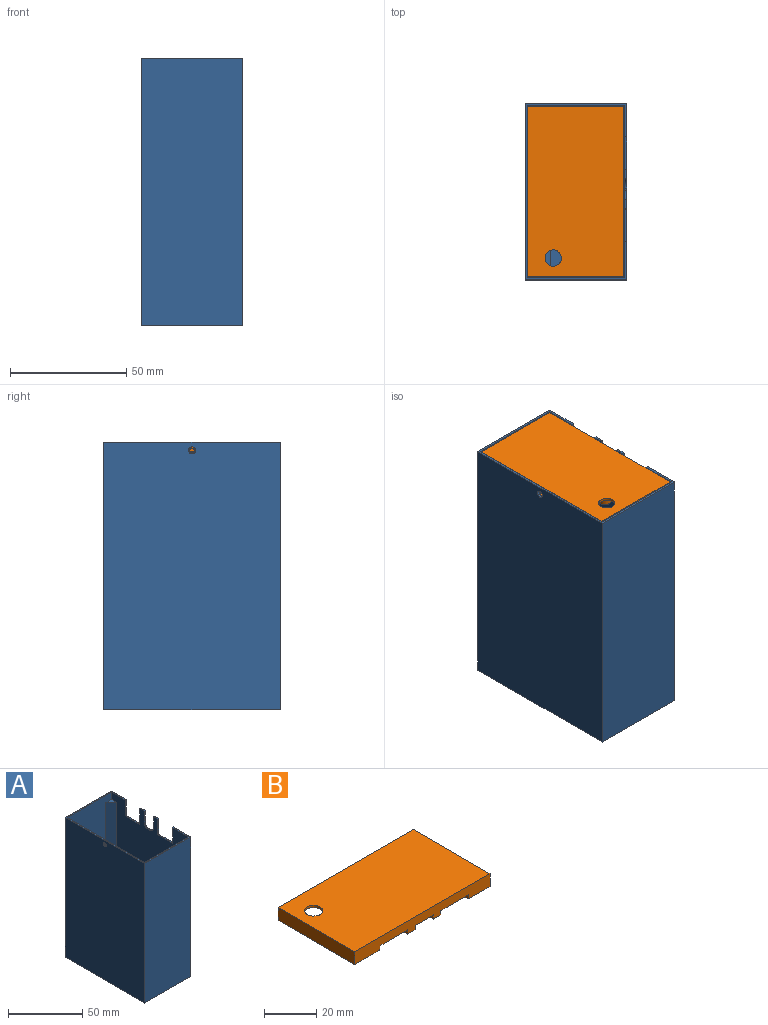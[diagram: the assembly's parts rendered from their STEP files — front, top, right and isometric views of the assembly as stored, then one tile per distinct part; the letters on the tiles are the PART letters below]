
ASSEMBLY  parts=2 mates=1
PART A: 180 faces, bbox 43.8x75.8x115 mm
  f0: plane 75.8x43.8mm, normal (0,0,-1), area 3281.9mm2, adj f6,f9,f10,f11,f41,f42,f43,f44
  f1: plane 75.8x43.8mm, normal (0,0,1), area 171.5mm2, adj f6,f9,f10,f11,f12,f13,f14,f15
  f2: plane 97.5x5mm, normal (0.71,-0.71,0), area 689.4mm2, adj f14,f15,f31,f40
  f3: plane 97.5x5mm, normal (-0.71,-0.71,0), area 689.4mm2, adj f13,f14,f33,f39
  f4: plane 97.5x5mm, normal (0.71,0.71,0), area 689.4mm2, adj f12,f15,f34,f38
  f5: plane 97.5x5mm, normal (-0.71,0.71,0), area 689.4mm2, adj f12,f13,f36,f37
  f6: plane 115x75.8mm, normal (1,0,0), area 8242.9mm2, adj f0,f1,f7,f8,f9,f10,f17,f18
  f7: plane 4x0.9mm, normal (0,0,1), area 3.6mm2, adj f6,f13,f17,f27
  f8: plane 4x0.9mm, normal (0,0,1), area 3.6mm2, adj f6,f13,f21,f22
  f9: plane 115x43.8mm, normal (0,-1,0), area 5037mm2, adj f0,f1,f6,f11
  f10: plane 115x43.8mm, normal (0,1,0), area 5037mm2, adj f0,f1,f6,f11
  f11: plane 115x75.8mm, normal (-1,0,0), area 8709.9mm2, adj f0,f1,f9,f10,f28
  f12: plane 108.5x42mm, normal (0,1,0), area 3521.3mm2, adj f1,f4,f5,f13,f15,f34,f35,f36
  f13: plane 103.5x74mm, normal (-1,0,0), area 6209.9mm2, adj f1,f3,f5,f7,f8,f12,f14,f17
  f14: plane 108.5x42mm, normal (0,-1,0), area 3521.3mm2, adj f1,f2,f3,f13,f15,f31,f32,f33
  f15: plane 103.5x74mm, normal (1,0,0), area 6676.9mm2, adj f1,f2,f4,f12,f14,f28,f30,f38
  f16: plane 64x22mm, normal (0,0,1), area 1408mm2, adj f29,f30,f32,f35
  f17: plane 9x0.9mm, normal (0,1,0), area 8.1mm2, adj f6,f7,f13,f18
  f18: cylinder r=4mm len=4mm, axis (1,0,0), area 5.7mm2, adj f6,f13,f17,f19
  f19: plane 1x0.9mm, normal (0,0,1), area 0.9mm2, adj f6,f13,f18,f20
  f20: cylinder r=4mm len=4mm, axis (1,0,0), area 5.7mm2, adj f6,f13,f19,f21
  f21: plane 9x0.9mm, normal (0,-1,0), area 8.1mm2, adj f6,f8,f13,f20
  f22: plane 13x0.9mm, normal (0,1,0), area 11.7mm2, adj f6,f8,f13,f23
  f23: plane 14x0.9mm, normal (0,0,1), area 12.6mm2, adj f6,f13,f22,f24
  f24: plane 13x0.9mm, normal (0,-1,0), area 11.7mm2, adj f1,f6,f13,f23
  f25: plane 13x0.9mm, normal (0,1,0), area 11.7mm2, adj f1,f6,f13,f26
  f26: plane 14x0.9mm, normal (0,0,1), area 12.6mm2, adj f6,f13,f25,f27
  f27: plane 13x0.9mm, normal (0,-1,0), area 11.7mm2, adj f6,f7,f13,f26
  f28: cylinder r=1.5mm len=3mm, axis (-1,0,0), area 8.5mm2, adj f11,f15
  f29: cylinder r=10mm len=64mm, axis (0,1,0), area 1005.3mm2, adj f13,f16,f33,f36
  f30: cylinder r=10mm len=64mm, axis (0,-1,0), area 1005.3mm2, adj f15,f16,f31,f34
  f31: cone r=5mm half-angle=45deg, axis (0,-1,0), area 83.3mm2, adj f2,f14,f30,f32
  f32: plane 22x5mm, normal (0,-0.71,0.71), area 155.6mm2, adj f14,f16,f31,f33
  f33: cone r=5mm half-angle=45deg, axis (0,-1,0), area 83.3mm2, adj f3,f14,f29,f32
  f34: cone r=5mm half-angle=45deg, axis (0,1,0), area 83.3mm2, adj f4,f12,f30,f35
  f35: plane 22x5mm, normal (0,0.71,0.71), area 155.6mm2, adj f12,f16,f34,f36
  f36: cone r=5mm half-angle=45deg, axis (0,1,0), area 83.3mm2, adj f5,f12,f29,f35
  f37: plane 5x5mm, normal (0,0,1), area 12.5mm2, adj f5,f12,f13
  f38: plane 5x5mm, normal (0,0,1), area 12.5mm2, adj f4,f12,f15
  f39: plane 5x5mm, normal (0,0,1), area 12.5mm2, adj f3,f13,f14
  f40: plane 5x5mm, normal (0,0,1), area 12.5mm2, adj f2,f14,f15
  f41: plane 0.85x0.5mm, normal (0,-1,0), area 0.4mm2, adj f0,f42,f54,f55
  f42: plane 3.17x0.5mm, normal (-1,0,0), area 1.6mm2, adj f0,f41,f43,f55
  f43: plane 0.6x0.5mm, normal (0,1,0), area 0.3mm2, adj f0,f42,f44,f55
  f44: plane 1.5x0.5mm, normal (1,0,0), area 0.7mm2, adj f0,f43,f45,f55
  f45: extruded ~0.87x0.5mm, area 0.4mm2, adj f0,f44,f46,f55
  f46: plane 0.5x0.02mm, normal (0,1,0), area 0mm2, adj f0,f45,f47,f55
  f47: plane 2.37x1.38mm, normal (-0.87,0.5,0), area 1.4mm2, adj f0,f46,f48,f55
  f48: plane 0.85x0.5mm, normal (0,1,0), area 0.4mm2, adj f0,f47,f49,f55
  f49: plane 3.17x0.5mm, normal (1,0,0), area 1.6mm2, adj f0,f48,f50,f55
  f50: plane 0.6x0.5mm, normal (0,-1,0), area 0.3mm2, adj f0,f49,f51,f55
  f51: plane 1.49x0.5mm, normal (-1,0,0), area 0.7mm2, adj f0,f50,f52,f55
  f52: extruded ~0.91x0.5mm, area 0.5mm2, adj f0,f51,f53,f55
  f53: plane 0.5x0.02mm, normal (0,-1,0), area 0mm2, adj f0,f52,f54,f55
  f54: plane 2.4x1.38mm, normal (0.87,-0.5,0), area 1.4mm2, adj f0,f41,f53,f55
  f55: plane 3.17x2.81mm, normal (0,0,-1), area 5.7mm2, adj f41,f42,f43,f44,f45,f46,f47,f48
  f56: plane 1.82x0.5mm, normal (0,-1,0), area 0.9mm2, adj f0,f57,f67,f68
  f57: plane 0.55x0.5mm, normal (-1,0,0), area 0.3mm2, adj f0,f56,f58,f68
  f58: plane 1.15x0.5mm, normal (0,1,0), area 0.6mm2, adj f0,f57,f59,f68
  f59: plane 0.82x0.5mm, normal (-1,0,0), area 0.4mm2, adj f0,f58,f60,f68
  f60: plane 1.07x0.5mm, normal (0,-1,0), area 0.5mm2, adj f0,f59,f61,f68
  f61: plane 0.55x0.5mm, normal (-1,0,0), area 0.3mm2, adj f0,f60,f62,f68
  f62: plane 1.07x0.5mm, normal (0,1,0), area 0.5mm2, adj f0,f61,f63,f68
  f63: plane 0.7x0.5mm, normal (-1,0,0), area 0.3mm2, adj f0,f62,f64,f68
  f64: plane 1.15x0.5mm, normal (0,-1,0), area 0.6mm2, adj f0,f63,f65,f68
  f65: plane 0.55x0.5mm, normal (-1,0,0), area 0.3mm2, adj f0,f64,f66,f68
  f66: plane 1.82x0.5mm, normal (0,1,0), area 0.9mm2, adj f0,f65,f67,f68
  f67: plane 3.17x0.5mm, normal (1,0,0), area 1.6mm2, adj f0,f56,f66,f68
  f68: plane 3.17x1.82mm, normal (0,0,-1), area 4mm2, adj f56,f57,f58,f59,f60,f61,f62,f63
  f69: extruded ~0.59x0.5mm, area 0.3mm2, adj f0,f70,f83,f84
  f70: extruded ~0.5x0.35mm, area 0.2mm2, adj f0,f69,f71,f84
  f71: extruded ~0.5x0.36mm, area 0.2mm2, adj f0,f70,f72,f84
  f72: plane 0.55x0.5mm, normal (-0.93,-0.37,0), area 0.3mm2, adj f0,f71,f73,f84
  f73: extruded ~0.93x0.5mm, area 0.5mm2, adj f0,f72,f74,f84
  f74: extruded ~0.79x0.5mm, area 0.4mm2, adj f0,f73,f75,f84
  f75: extruded ~0.57x0.52mm, area 0.4mm2, adj f0,f74,f76,f84
  f76: extruded ~0.87x0.5mm, area 0.4mm2, adj f0,f75,f77,f84
  f77: extruded ~1.2x0.5mm, area 0.6mm2, adj f0,f76,f78,f84
  f78: extruded ~1.06x0.5mm, area 0.6mm2, adj f0,f77,f79,f84
  f79: extruded ~0.87x0.5mm, area 0.4mm2, adj f0,f78,f80,f84
  f80: plane 0.56x0.5mm, normal (-1,0,0), area 0.3mm2, adj f0,f79,f81,f84
  f81: extruded ~0.81x0.5mm, area 0.4mm2, adj f0,f80,f82,f84
  f82: extruded ~1.06x0.8mm, area 0.8mm2, adj f0,f81,f83,f84
  f83: extruded ~0.79x0.5mm, area 0.4mm2, adj f0,f69,f82,f84
  f84: plane 3.26x2.41mm, normal (0,0,-1), area 3.5mm2, adj f69,f70,f71,f72,f73,f74,f75,f76
  f85: plane 1.82x0.5mm, normal (0,-1,0), area 0.9mm2, adj f0,f86,f96,f97
  f86: plane 0.55x0.5mm, normal (-1,0,0), area 0.3mm2, adj f0,f85,f87,f97
  f87: plane 1.15x0.5mm, normal (0,1,0), area 0.6mm2, adj f0,f86,f88,f97
  f88: plane 0.82x0.5mm, normal (-1,0,0), area 0.4mm2, adj f0,f87,f89,f97
  f89: plane 1.07x0.5mm, normal (0,-1,0), area 0.5mm2, adj f0,f88,f90,f97
  f90: plane 0.55x0.5mm, normal (-1,0,0), area 0.3mm2, adj f0,f89,f91,f97
  f91: plane 1.07x0.5mm, normal (0,1,0), area 0.5mm2, adj f0,f90,f92,f97
  f92: plane 0.7x0.5mm, normal (-1,0,0), area 0.3mm2, adj f0,f91,f93,f97
  f93: plane 1.15x0.5mm, normal (0,-1,0), area 0.6mm2, adj f0,f92,f94,f97
  f94: plane 0.55x0.5mm, normal (-1,0,0), area 0.3mm2, adj f0,f93,f95,f97
  f95: plane 1.82x0.5mm, normal (0,1,0), area 0.9mm2, adj f0,f94,f96,f97
  f96: plane 3.17x0.5mm, normal (1,0,0), area 1.6mm2, adj f0,f85,f95,f97
  f97: plane 3.17x1.82mm, normal (0,0,-1), area 4mm2, adj f85,f86,f87,f88,f89,f90,f91,f92
  f98: plane 1.22x0.5mm, normal (-1,0,0), area 0.6mm2, adj f0,f99,f116,f117
  f99: plane 0.5x0.36mm, normal (0,-1,0), area 0.2mm2, adj f0,f98,f100,f117
  f100: plane 1.22x0.76mm, normal (0.85,-0.53,0), area 0.7mm2, adj f0,f99,f101,f117
  f101: plane 0.75x0.5mm, normal (0,-1,0), area 0.4mm2, adj f0,f100,f102,f117
  f102: extruded ~1.38x0.93mm, area 0.8mm2, adj f0,f101,f103,f117
  f103: extruded ~0.5x0.44mm, area 0.3mm2, adj f0,f102,f104,f117
  f104: extruded ~0.5x0.5mm, area 0.3mm2, adj f0,f103,f105,f117
  f105: extruded ~0.71x0.5mm, area 0.4mm2, adj f0,f104,f106,f117
  f106: extruded ~0.96x0.5mm, area 0.5mm2, adj f0,f105,f107,f117
  f107: plane 0.92x0.5mm, normal (0,1,0), area 0.5mm2, adj f0,f106,f108,f117
  f108: plane 3.17x0.5mm, normal (1,0,0), area 1.6mm2, adj f0,f107,f116,f117
  f109: plane 0.5x0.22mm, normal (0,1,0), area 0.1mm2, adj f110,f115,f117,f118
  f110: plane 0.86x0.5mm, normal (-1,0,0), area 0.4mm2, adj f109,f111,f117,f118
  f111: plane 0.5x0.2mm, normal (0,-1,0), area 0.1mm2, adj f110,f112,f117,f118
  f112: extruded ~0.5x0.48mm, area 0.2mm2, adj f111,f113,f117,f118
  f113: extruded ~0.5x0.32mm, area 0.2mm2, adj f112,f114,f117,f118
  f114: extruded ~0.5x0.33mm, area 0.2mm2, adj f113,f115,f117,f118
  f115: extruded ~0.5x0.47mm, area 0.2mm2, adj f109,f114,f117,f118
  f116: plane 0.67x0.5mm, normal (0,-1,0), area 0.3mm2, adj f0,f98,f108,f117
  f117: plane 3.17x2.53mm, normal (0,0,-1), area 4.9mm2, adj f98,f99,f100,f101,f102,f103,f104,f105
  f118: plane 0.86x0.84mm, normal (0,0,-1), area 0.6mm2, adj f109,f110,f111,f112,f113,f114,f115
  f119: extruded ~0.8x0.5mm, area 0.4mm2, adj f120,f132,f133,f179
  f120: extruded ~0.8x0.5mm, area 0.4mm2, adj f119,f121,f133,f179
  f121: extruded ~0.6x0.5mm, area 0.3mm2, adj f120,f122,f133,f179
  f122: extruded ~1.07x0.8mm, area 0.8mm2, adj f121,f123,f133,f179
  f123: extruded ~1.07x0.8mm, area 0.8mm2, adj f122,f132,f133,f179
  f124: extruded ~1.21x0.5mm, area 0.7mm2, adj f0,f125,f131,f133
  f125: extruded ~1.21x0.5mm, area 0.6mm2, adj f0,f124,f126,f133
  f126: extruded ~1.12x0.5mm, area 0.6mm2, adj f0,f125,f127,f133
  f127: extruded ~1.12x0.5mm, area 0.6mm2, adj f0,f126,f128,f133
  f128: extruded ~1.21x0.5mm, area 0.7mm2, adj f0,f127,f129,f133
  f129: extruded ~1.21x0.5mm, area 0.7mm2, adj f0,f128,f130,f133
  f130: extruded ~1.12x0.5mm, area 0.6mm2, adj f0,f129,f131,f133
  f131: extruded ~1.12x0.5mm, area 0.6mm2, adj f0,f124,f130,f133
  f132: extruded ~0.6x0.5mm, area 0.3mm2, adj f119,f123,f133,f179
  f133: plane 3.26x3.02mm, normal (0,0,-1), area 5.3mm2, adj f119,f120,f121,f122,f123,f124,f125,f126
  f134: extruded ~0.68x0.5mm, area 0.4mm2, adj f0,f135,f161,f162
  f135: extruded ~0.52x0.5mm, area 0.3mm2, adj f0,f134,f136,f162
  f136: extruded ~0.61x0.5mm, area 0.4mm2, adj f0,f135,f137,f162
  f137: extruded ~0.5x0.43mm, area 0.2mm2, adj f0,f136,f138,f162
  f138: extruded ~0.5x0.13mm, area 0.1mm2, adj f0,f137,f139,f162
  f139: extruded ~0.5x0.16mm, area 0.1mm2, adj f0,f138,f140,f162
  f140: extruded ~0.5x0.23mm, area 0.1mm2, adj f0,f139,f141,f162
  f141: extruded ~0.5x0.29mm, area 0.2mm2, adj f0,f140,f142,f162
  f142: extruded ~0.5x0.33mm, area 0.2mm2, adj f0,f141,f143,f162
  f143: extruded ~0.5x0.42mm, area 0.2mm2, adj f0,f142,f144,f162
  f144: plane 0.52x0.5mm, normal (-0.92,-0.38,0), area 0.3mm2, adj f0,f143,f145,f162
  f145: extruded ~0.5x0.47mm, area 0.2mm2, adj f0,f144,f146,f162
  f146: extruded ~0.5x0.47mm, area 0.2mm2, adj f0,f145,f147,f162
  f147: extruded ~0.79x0.5mm, area 0.4mm2, adj f0,f146,f148,f162
  f148: extruded ~0.66x0.5mm, area 0.4mm2, adj f0,f147,f149,f162
  f149: extruded ~0.5x0.39mm, area 0.2mm2, adj f0,f148,f150,f162
  f150: extruded ~0.5x0.29mm, area 0.2mm2, adj f0,f149,f151,f162
  f151: extruded ~0.5x0.44mm, area 0.3mm2, adj f0,f150,f152,f162
  f152: extruded ~0.5x0.41mm, area 0.2mm2, adj f0,f151,f153,f162
  f153: extruded ~0.5x0.15mm, area 0.1mm2, adj f0,f152,f154,f162
  f154: extruded ~0.5x0.17mm, area 0.1mm2, adj f0,f153,f155,f162
  f155: extruded ~0.5x0.25mm, area 0.1mm2, adj f0,f154,f156,f162
  f156: extruded ~0.5x0.34mm, area 0.2mm2, adj f0,f155,f157,f162
  f157: extruded ~0.5x0.41mm, area 0.2mm2, adj f0,f156,f158,f162
  f158: extruded ~0.54x0.5mm, area 0.3mm2, adj f0,f157,f159,f162
  f159: plane 0.62x0.5mm, normal (1,0,0), area 0.3mm2, adj f0,f158,f160,f162
  f160: extruded ~0.9x0.5mm, area 0.5mm2, adj f0,f159,f161,f162
  f161: extruded ~0.86x0.5mm, area 0.5mm2, adj f0,f134,f160,f162
  f162: plane 3.26x2.07mm, normal (0,0,-1), area 3.8mm2, adj f134,f135,f136,f137,f138,f139,f140,f141
  f163: extruded ~0.59x0.5mm, area 0.3mm2, adj f0,f164,f177,f178
  f164: extruded ~0.5x0.35mm, area 0.2mm2, adj f0,f163,f165,f178
  f165: extruded ~0.5x0.36mm, area 0.2mm2, adj f0,f164,f166,f178
  f166: plane 0.55x0.5mm, normal (-0.93,-0.37,0), area 0.3mm2, adj f0,f165,f167,f178
  f167: extruded ~0.93x0.5mm, area 0.5mm2, adj f0,f166,f168,f178
  f168: extruded ~0.79x0.5mm, area 0.4mm2, adj f0,f167,f169,f178
  f169: extruded ~0.57x0.52mm, area 0.4mm2, adj f0,f168,f170,f178
  f170: extruded ~0.87x0.5mm, area 0.4mm2, adj f0,f169,f171,f178
  f171: extruded ~1.2x0.5mm, area 0.6mm2, adj f0,f170,f172,f178
  f172: extruded ~1.06x0.5mm, area 0.6mm2, adj f0,f171,f173,f178
  f173: extruded ~0.87x0.5mm, area 0.4mm2, adj f0,f172,f174,f178
  f174: plane 0.56x0.5mm, normal (-1,0,0), area 0.3mm2, adj f0,f173,f175,f178
  f175: extruded ~0.81x0.5mm, area 0.4mm2, adj f0,f174,f176,f178
  f176: extruded ~1.06x0.8mm, area 0.8mm2, adj f0,f175,f177,f178
  f177: extruded ~0.79x0.5mm, area 0.4mm2, adj f0,f163,f176,f178
  f178: plane 3.26x2.41mm, normal (0,0,-1), area 3.5mm2, adj f163,f164,f165,f166,f167,f168,f169,f170
  f179: plane 2.14x1.61mm, normal (0,0,-1), area 2.9mm2, adj f119,f120,f121,f122,f123,f132
PART B: 42 faces, bbox 73.2x41.6x6 mm
  f0: plane 70x5mm, normal (0,1,0), area 266mm2, adj f1,f2,f3,f8,f10,f14,f28,f29
  f1: plane 4x1.6mm, normal (0,0,-1), area 6.4mm2, adj f0,f5,f35,f39
  f2: plane 4x1.6mm, normal (0,0,-1), area 6.4mm2, adj f0,f5,f32,f36
  f3: plane 66x36.4mm, normal (0,0,-1), area 2283.6mm2, adj f0,f6,f23,f25,f26,f27,f28,f29
  f4: plane 32.5x3mm, normal (0,-1,0), area 97.5mm2, adj f10,f14,f23,f30
  f5: plane 73.2x6mm, normal (0,-1,0), area 359.2mm2, adj f1,f2,f7,f11,f12,f14,f31,f32
  f6: cylinder r=3.5mm len=7mm, axis (0,0,-1), area 22mm2, adj f3,f7
  f7: plane 73.2x41.6mm, normal (0,0,1), area 3006.6mm2, adj f5,f6,f11,f12,f13
  f8: plane 38.4x3mm, normal (-1,0,0), area 115.2mm2, adj f0,f9,f14,f28
  f9: plane 32.5x3mm, normal (0,-1,0), area 97.5mm2, adj f8,f14,f25,f27
  f10: plane 38.4x3mm, normal (1,0,0), area 115.2mm2, adj f0,f4,f14,f29
  f11: plane 41.6x6mm, normal (-1,0,0), area 249.6mm2, adj f5,f7,f13,f14
  f12: plane 41.6x6mm, normal (1,0,0), area 249.6mm2, adj f5,f7,f13,f14
  f13: plane 73.2x6mm, normal (0,1,0), area 436.1mm2, adj f7,f11,f12,f14,f24
  f14: plane 73.2x41.6mm, normal (0,0,-1), area 305.3mm2, adj f0,f4,f5,f8,f9,f10,f11,f12
  f15: cylinder r=1mm len=3mm, axis (0,0,1), area 18.8mm2, adj f17,f18
  f16: cylinder r=2.5mm len=5mm, axis (0,0,1), area 31.4mm2, adj f17,f41
  f17: plane 5x5mm, normal (0,0,-1), area 16.5mm2, adj f15,f16
  f18: plane 2x2mm, normal (0,0,-1), area 3.1mm2, adj f15
  f19: cylinder r=1mm len=3mm, axis (0,0,1), area 18.8mm2, adj f21,f22
  f20: cylinder r=2.5mm len=5mm, axis (0,0,1), area 30.7mm2, adj f21,f28,f40
  f21: plane 5x5mm, normal (0,0,-1), area 16.5mm2, adj f19,f20
  f22: plane 2x2mm, normal (0,0,-1), area 3.1mm2, adj f19
  f23: plane 5x5mm, normal (-1,0,0), area 23mm2, adj f3,f4,f14,f26,f30
  f24: cylinder r=1mm len=6.6mm, axis (0,1,0), area 41.5mm2, adj f13,f26
  f25: plane 5x5mm, normal (1,0,0), area 23mm2, adj f3,f9,f14,f26,f27
  f26: plane 5x5mm, normal (0,-1,0), area 21.9mm2, adj f3,f14,f23,f24,f25
  f27: plane 32.5x2mm, normal (0,-0.71,-0.71), area 89.1mm2, adj f3,f9,f25,f28
  f28: plane 38.4x2mm, normal (-0.71,0,-0.71), area 97.7mm2, adj f0,f3,f8,f20,f27,f40
  f29: plane 38.4x2mm, normal (0.71,0,-0.71), area 105.8mm2, adj f0,f3,f10,f30
  f30: plane 32.5x2mm, normal (0,-0.71,-0.71), area 89.1mm2, adj f3,f4,f23,f29
  f31: plane 15x1.6mm, normal (0,0,-1), area 24mm2, adj f0,f5,f32,f33
  f32: plane 2x1.6mm, normal (1,0,0), area 3.2mm2, adj f0,f2,f5,f31
  f33: plane 2x1.6mm, normal (-1,0,0), area 3.2mm2, adj f0,f5,f14,f31
  f34: plane 10x1.6mm, normal (0,0,-1), area 16mm2, adj f0,f5,f35,f36
  f35: plane 2x1.6mm, normal (1,0,0), area 3.2mm2, adj f0,f1,f5,f34
  f36: plane 2x1.6mm, normal (-1,0,0), area 3.2mm2, adj f0,f2,f5,f34
  f37: plane 15x1.6mm, normal (0,0,-1), area 24mm2, adj f0,f5,f38,f39
  f38: plane 2x1.6mm, normal (1,0,0), area 3.2mm2, adj f0,f5,f14,f37
  f39: plane 2x1.6mm, normal (-1,0,0), area 3.2mm2, adj f0,f1,f5,f37
  f40: cone r=3.5mm half-angle=45deg, axis (0,0,1), area 18.2mm2, adj f3,f20,f28
  f41: cone r=3.5mm half-angle=45deg, axis (0,0,1), area 26.7mm2, adj f3,f16
PLACE A t=(-31.83,-6.04,-1.68)mm
PLACE B rot(axis=(0,0,1),90deg) t=(8.77,-3.04,112.32)mm
MATE fastened B.f13 <-> A.f15  axis (-1,0,0) through (-31.83,30.96,113.32)mm
